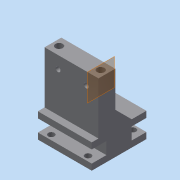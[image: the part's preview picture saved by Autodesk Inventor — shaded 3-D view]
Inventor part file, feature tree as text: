
AUTODESK INVENTOR PART (.ipt)
format: ipt  version: 2015 (Build 190159000, 159)  size: 205,824 bytes
history: native  units: mm
features: sketch x12, extrude x9, projected_geometry x5, hole x3, plane x1, chamfer x1
ambient origin geometry x8: Origin, YZ Plane, XZ Plane, XY Plane, X Axis, Y Axis, Z Axis, Center Point
bodies: Solid1 (feature_tree)
feature tree (31):
  extrude  "Extrusion1"  Depth=6.0mm
  hole  "Hole1"  [1 undecoded]
  hole  "Hole2"  [1 undecoded]
  extrude  "Extrusion2"  Depth=10.0mm
  extrude  "Extrusion3"  Depth=10.0mm
  plane  "Work Plane1"
  extrude  "Extrusion4"  Depth=10.0mm
  hole  "Hole3"  [1 undecoded]
  extrude  "Extrusion5"  Depth=10.0mm
  chamfer  "Chamfer1"  Distance=10.0mm
  extrude  "Extrusion6"  Depth=2.0mm
  extrude  "Extrusion7"  Depth=2.0mm
  extrude  "Extrusion8"  Depth=2.0mm
  extrude  "Extrusion9"  Depth=2.0mm
  sketch  "Sketch1"  dims[d0=6.0mm d1=6.0mm]
  sketch  "Sketch2"  dims[d2=34.0mm d3=44.0mm]
  sketch  "Sketch3"  dims[d4=5.0mm d5=42.5mm d6=0.0mm]
  sketch  "Sketch4"  dims[d10=4.0mm d11=6.0mm d12=4.0mm d13=2.0mm d14=90.0deg d15=10.0mm d16=20.594885mm d17=10.0mm]
  projected_geometry  "Projected Loop1"
  sketch  "Sketch5"  dims[d18=11.0mm d19=10.0mm]
  sketch  "Sketch6"  dims[d20=10.0mm]
  sketch  "Sketch7"  dims[d21=4.0mm d22=6.0mm d23=4.0mm d24=2.0mm d25=90.0deg d26=10.0mm d27=20.594885mm d28=7.5mm]
  sketch  "Sketch8"  dims[d29=27.5mm d30=20.0mm d31=0.0mm]
  sketch  "Sketch9"  dims[d32=20.0mm d33=0.0mm d34=10.0mm]
  projected_geometry  "Projected Loop2"
  sketch  "Sketch10"  dims[d35=5.0mm]
  projected_geometry  "Projected Loop3"
  sketch  "Sketch11"  dims[d36=12.0mm]
  projected_geometry  "Projected Loop4"
  sketch  "Sketch12"  dims[d37=12.0mm d38=10.0mm d39=0.0mm d40=4.0mm d41=4.0mm d42=4.0mm d43=4.0mm d44=7.0mm d45=7.0mm d46=7.0mm d47=7.0mm d48=4.0mm d49=6.0mm d50=5.0mm d51=6.0mm d52=90.0deg d53=16.0mm d54=20.594885mm d55=0.0mm d56=5.0mm d57=15.5mm d58=0.0mm d59=15.5mm d60=2.0mm d61=45.0deg d62=15.5mm d63=0.0mm d64=2.0mm d65=0.0mm d66=2.0mm d67=0.0mm d68=2.0mm d69=0.0mm]
  projected_geometry  "Projected Loop5"
note: 3 required parameter values undecoded (feature->parameter linkage not recoverable at this tier; creation-order binding heuristic only, values carry confidence <= 0.55)
